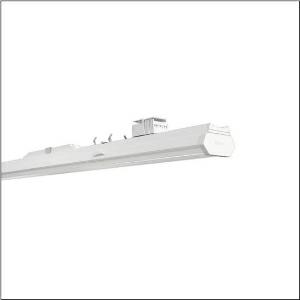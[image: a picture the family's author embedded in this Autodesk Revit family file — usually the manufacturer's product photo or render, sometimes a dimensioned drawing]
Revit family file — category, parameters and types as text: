
# Revit family: licross_r__11_protected_mo_51td1b7n48xg_edd2
name_source: partatom
category: Lighting Fixtures
units: mm (PartAtom-declared; Revit-internal decimal feet)

## family parameters
Cut with Voids When Loaded = No
Host = Face
Light Source = No
Part Type = Normal
Room Calculation Point = No
Round Connector Dimension = Use Diameter
Shared = No

## types (1)
- Licross® 11 Protected MO (1 x LED, 8190 lm, 48.6 W, 4000K)
    Apparent Load = 49 VA
    CIE Flux Codes = 54 82 95 97 100
    Color Rendering = 80
    Color Temperature = 4000K
    Default Elevation = 1800 mm
    Description = Licross® 11 Protected MO, luminaire insert, of sheet steel, galvanised, coil coated, white, length: 1.500mm, width: 90mm, height: 101mm, LED rated luminous flux: 8.190lm, light colour: 840, control gear: ON/OFF, with plug, 3-pole, with phase selection, mains connection: 220..240V, AC, 50/60Hz, rated input power: 49W, internal wiring halogen-free, primary optical cover: cover, of PMMA, light emission: direct distribution, primary light characteristic: symmetric, protection rating (complete): IP54, insulation class (complete): insulation class I (protective earthing), certification: CE, ENEC, VDE, UKCA, protection symbol: D if used in an environment with non-conductive dust loads with corresponding accessories, impact resistance: IK06, permissible ambient temperature for indoor applications: -25..+35°C, corresponds to IFS (International Featured Standards) requirements for safety and quality in the food industry, reducing of maximum allowable ambient temperature of 5°C with ceiling mounting, LABS conformity tested according to VDMA 24364:2018-05, packaging unit: 1 piece
    Height = 92 mm
    Lamp = 1 x LED
    Lamp Light Flux = 8190 lm
    Lamp Power = 48.6 W
    Lamp count = 1
    Length = 1500 mm
    Luminous efficacy = 169 lm/W
    Manufacturer = Siteco
    ModVariant = No
    Model = 51TD1B7N48XG
    Mounting Place = Ceiling
    Mounting Type = Pendant
    Number of Poles = 1
    OnlyDefault = Yes
    Power Factor = 1
    Product Name = Licross® 11 Protected MO
    Product group = luminaire insert | ceiling pendant
    ProductGroupID = 902
    Protection Class = Protection class I
    Protection Degree = IP 54
    RLX_Detail_Level = 1
    RLX_Emergency_Light_Flux = 0 lm
    RLX_Emergency_Type = 0
    RLX_Emergency_Type_DB = No
    RlxData = <blob elided: 20629 chars, md5=3fd0d6ba>
    Socket = socket
    Standby Power = 0 W
    System Light Flux = 8190 lm
    System Power = 49 W
    Type Comments = Product without accessories
    Type Image = l_1256145.jpg
    URL = http://relux.com
    VarID = ---
    Voltage = 0 V
    Weight = 0.00 kg
    Width = 88 mm

## geometry (parser evidence)
native form markers: Blend x4, Sweep x10
no freeform markers — native parametric forms only
